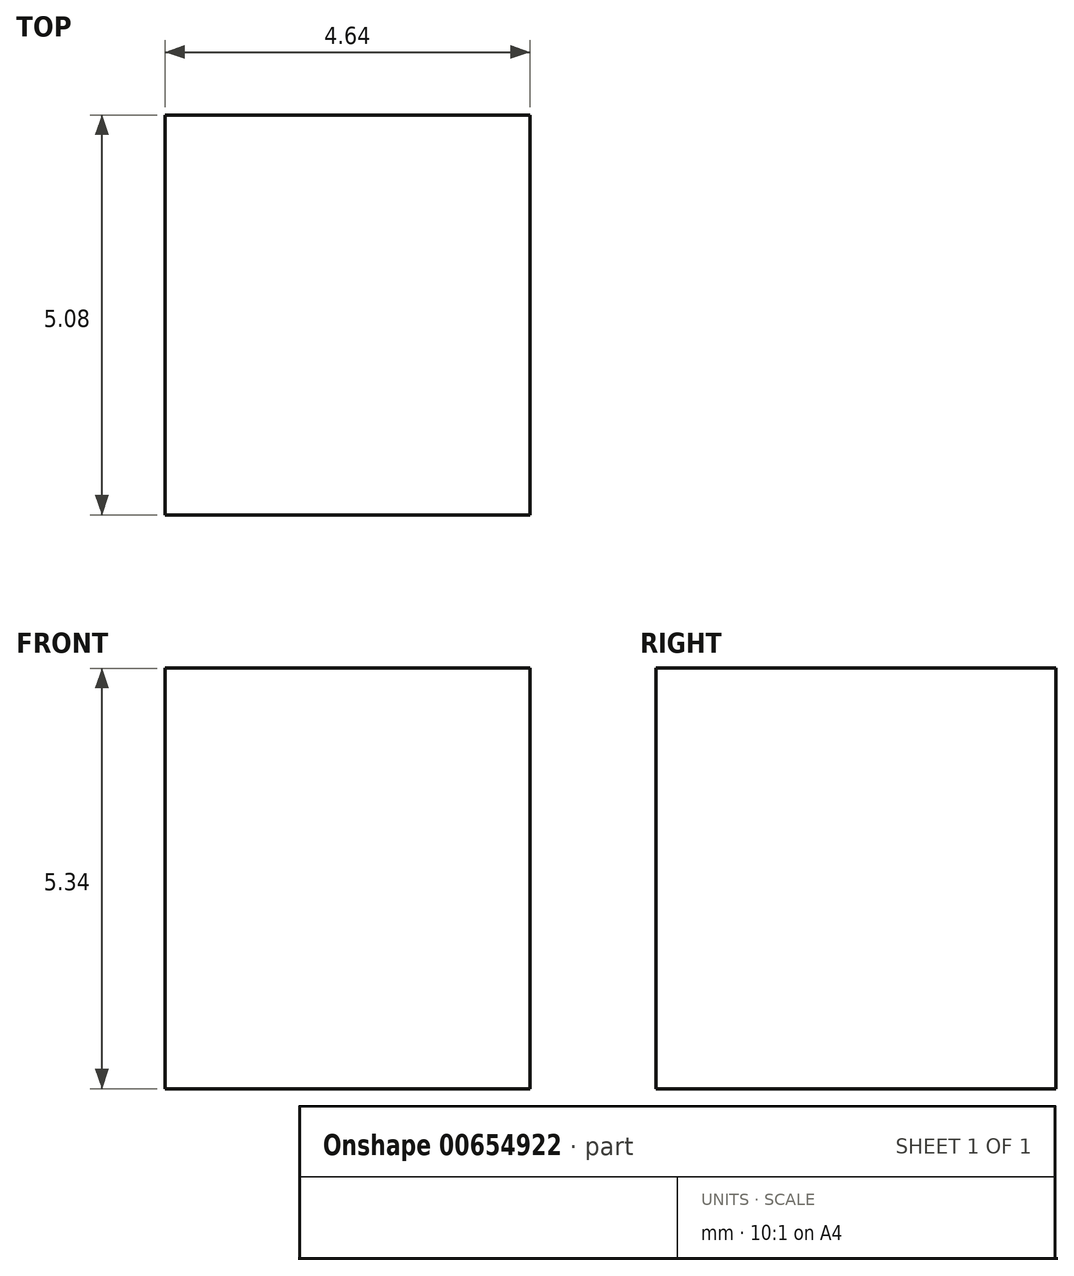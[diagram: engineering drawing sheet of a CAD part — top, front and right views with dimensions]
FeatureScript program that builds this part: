
annotation { "Feature Type Name" : "Feature", "Feature Type Description" : "" }
export const myFeature = defineFeature(function(context is Context, id is Id, definition is map)
    precondition{}
    {
        {
            var Q0;
            Q0=qCreatedBy(makeId("Front.planeOp"),FACE);
            var sketch = newSketch(context, id + "F0", { "sketchPlane" : qUnion([Q0])});
            skLineSegment(sketch, "E0", {"start": v(0, 0) * mm, "end": v(4.64, 0) * mm});
            skLineSegment(sketch, "E1", {"start": v(4.64, 0) * mm, "end": v(4.64, 5.34) * mm});
            skLineSegment(sketch, "E2", {"start": v(4.64, 5.34) * mm, "end": v(0, 5.34) * mm});
            skLineSegment(sketch, "E3", {"start": v(0, 5.34) * mm, "end": v(0, 0) * mm});
            skSolve(sketch);
        }
        {
            var Q0;
            Q0=makeQuery(id+"F0.imprint","IMPRINT",FACE,{"disambiguationData":[TD([[makeQuery(id+"F0.imprint","IMPRINT",EDGE,{"derivedFrom":sQuery(id+"F0.wireOp",EDGE,"E0")}),1.0]])]});
            extrude(context, id + "F1", {"entities" : qUnion([Q0]), "depth" : 5.08 * mm, "offsetDistance" : 25.4 * mm});
        }
    });
